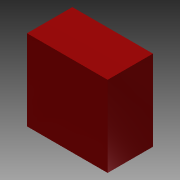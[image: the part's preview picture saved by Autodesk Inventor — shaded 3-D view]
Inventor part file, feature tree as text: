
AUTODESK INVENTOR PART (.ipt)
format: ipt  version: 2015 (Build 190159000, 159)  size: 88,064 bytes
history: native  units: in
note: dims shown in document units (in); Inventor stores cm internally (conversion verified against a paired STEP export)
features: extrude x2, sketch x2
ambient origin geometry x8: Origin, YZ Plane, XZ Plane, XY Plane, X Axis, Y Axis, Z Axis, Center Point
bodies: Solid1 (feature_tree)
feature tree (4):
  extrude  "BLOK"  Depth=0.6299in
  extrude  "USBGAT"  Depth=0.0787in
  sketch  "Sketch1"  dims[d0=0.6299in d1=0.6299in]
  sketch  "Sketch3"  dims[d4=0.3543in d5=0.0in d21=0.0787in d22=0.0394in d23=0.0394in d24=0.1969in d25=0.4724in d26=0.0in]
